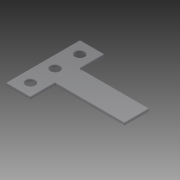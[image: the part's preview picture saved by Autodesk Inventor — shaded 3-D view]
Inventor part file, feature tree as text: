
AUTODESK INVENTOR PART (.ipt)
format: ipt  version: 2014 SP1 (Build 180222100, 222)  size: 176,640 bytes
history: native  units: in
note: dims shown in document units (in); Inventor stores cm internally (conversion verified against a paired STEP export)
features: extrude x4, sketch x4, fillet x1
ambient origin geometry x8: Origin, YZ Plane, XZ Plane, XY Plane, X Axis, Y Axis, Z Axis, Center Point
bodies: Solid1 (feature_tree)
feature tree (9):
  extrude  "Extrusion1"  Depth=0.5in
  extrude  "Extrusion2"  Depth=2.0in
  extrude  "Extrusion3"  Depth=0.0625in TaperAngle=0.0deg
  extrude  "Extrusion4"  Depth=0.015in
  fillet  "Fillet2"  Radius=0.0625in
  sketch  "Sketch1"  dims[d2=0.5in d4=0.7in]
  sketch  "Sketch2"  dims[d5=2.0in d6=2.0in]
  sketch  "Sketch3"  dims[d7=0.1825in d9=0.0625in d10=0.0in]
  sketch  "Sketch4"  dims[d11=0.25in d12=0.182in d16=0.0625in d17=0.0in d19=0.5in d20=1.1811in d22=0.5in d23=0.3937in d25=1.0in d27=0.2in d28=0.0625in d29=0.0in d30=0.0625in d31=0.0in d32=0.015in]
